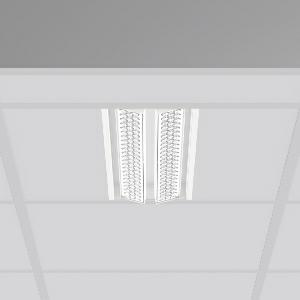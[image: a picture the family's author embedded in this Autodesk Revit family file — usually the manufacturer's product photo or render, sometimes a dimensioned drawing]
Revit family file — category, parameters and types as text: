
# Revit family: tx-move_901734_002_3_76_1a37
name_source: partatom
category: Lighting Fixtures
units: mm (PartAtom-declared; Revit-internal decimal feet)

## family parameters
Cut with Voids When Loaded = No
Host = Face
Light Source = No
Part Type = Normal
Room Calculation Point = No
Round Connector Dimension = Use Diameter
Shared = No

## types (1)
- MultiLumen 1 (1 x LED Modul 835, 2650 lm, 3500)
    Apparent Load = 35 VA
    CIE Flux Codes = 65 90 98 100 100
    Color Rendering = 80
    Color Temperature = 3500
    Default Elevation = 1800 mm
    Description = Series: TX-MOVE
Einlege/Einbau-Flächenstrahler. Housing: sheet steel, powder-coated. 2xSwivel range: 90°. High-efficiency LED units with optimum light control thanks to clear plastic (PC) lens optics. Spezielle Mikrostrukturen reduzieren Gelbsaum. Asymmetrical light distribution. Suitable for laying in grid ceiling module 600. Connected converter included in separate gearbox.Suitable for through-wiring.MultiLumen: Luminous flux adjustable in 3 steps. Accessories: Mounting frame for installation in suspended ceilings. Environmentally friendly and resource-saving due to replaceable and recyclable components. 
Colour: traffic white, matt (RAL 9016)
Length: 597 mm
Width: 190 mm
Height: 39 mm
Cut-out length: 577.5 mm
Cut-out width: 174 mm
Recess height: 100 mm
Lamp: LED
Socket: without socket
Colour temperature: 3500K
Colour rendering index (CRI): 80
System power: 35 W
Rated luminous flux: 5300 lm
Luminous efficiency: 151 lm/W
System power 2: 47 W
Rated luminous flux 2: 6900 lm
Luminous efficiency 2: 147 lm/W
System power 3: 68 W
Rated luminous flux 3: 9450 lm
Luminous efficiency 3: 139 lm/W
Control gear: Dimmable EVG, DALI
Protection class: I
Type of protection: IP 20
    Height = 0 mm  [stored 0 ft]
    Lamp = 1 x LED Modul 835
    Lamp Light Flux = 2650 lm
    Lamp count = 1
    Length = 597 mm
    Lifetime = 50000 h
    Luminous efficacy = 151 lm/W
    Manufacturer = RZB
    ModVariant = No
    Model = 901734.002.3.76
    Mounting Place = Ceiling, Wall
    Mounting Type = Recessed
    Number of Poles = 1
    OnlyDefault = Yes
    Power Factor = 1
    Product Name = TX-MOVE
    Product group = Recessed projectors
    ProductGroupID = 401
    Protection Class = Protection class I
    Protection Degree = IP 20
    RLX_Detail_Level = 1
    RLX_Emergency_Light_Flux = 0 lm
    RLX_Emergency_Type = 0
    RLX_Emergency_Type_DB = No
    RlxData = <blob elided: 56041 chars, md5=c1d11210>
    Socket = socket
    Standby Power = 0 W
    System Light Flux = 5300 lm
    System Power = 35 W
    Type Comments = MultiLumen 1
    Type Image = 901733.002.jpg
    URL = http://relux.com
    VarID = multilumen_1
    Voltage = 230 V
    Voltage Range = 220-240 V
    Weight = 0.00 kg
    Width = 190 mm  [stored 0.62336 ft]

note: [stored X ft] marks values corroborated as IEEE doubles in the binary element streams (Revit-internal decimal feet)

## geometry (parser evidence)
native form markers: Blend x4, Sweep x18
no freeform markers — native parametric forms only
